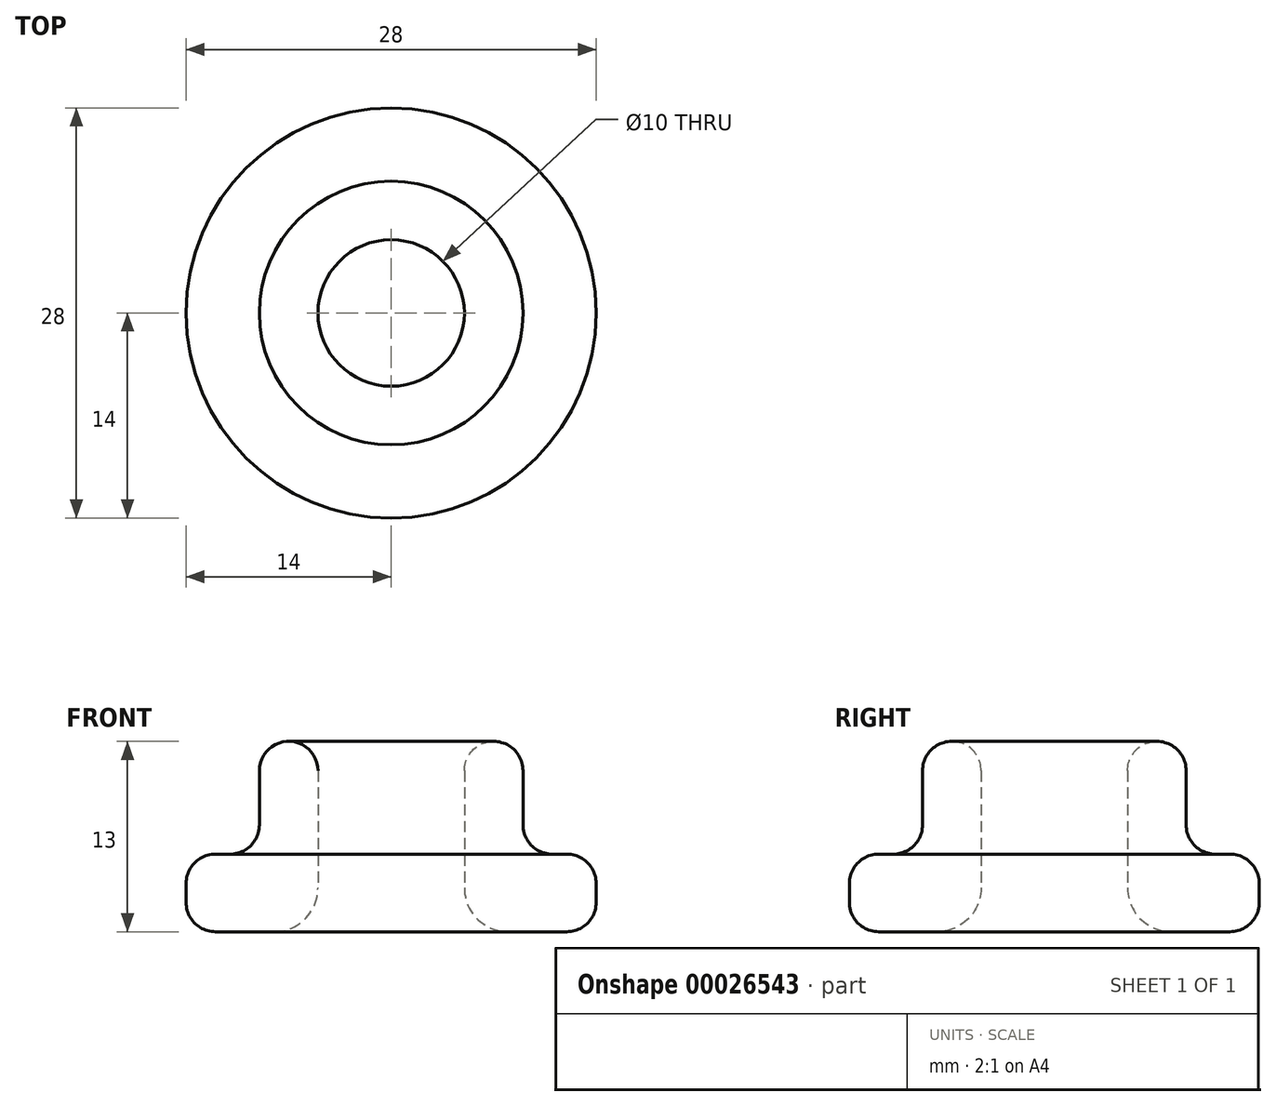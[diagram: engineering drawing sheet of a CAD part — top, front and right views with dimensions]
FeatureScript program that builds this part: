
annotation { "Feature Type Name" : "Feature", "Feature Type Description" : "" }
export const myFeature = defineFeature(function(context is Context, id is Id, definition is map)
    precondition{}
    {
        {
            var Q0;
            Q0=qCreatedBy(makeId("Front.planeOp"),FACE);
            var sketch = newSketch(context, id + "F0", { "sketchPlane" : qUnion([Q0])});
            skLineSegment(sketch, "E0", {"start": v(8, 0) * mm, "end": v(12, 0) * mm});
            skLineSegment(sketch, "E1", {"start": v(14, 2) * mm, "end": v(14, 3.3) * mm});
            skLineSegment(sketch, "E2", {"start": v(12, 5.3) * mm, "end": v(11, 5.3) * mm});
            skLineSegment(sketch, "E3", {"start": v(9, 7.3) * mm, "end": v(9, 11) * mm});
            skLineSegment(sketch, "E4", {"start": v(5, 11) * mm, "end": v(5, 3) * mm});
            skLineSegment(sketch, "E5", {"start": v(0, 0) * mm, "end": v(0, 27.16) * mm, "construction": true});
            skPoint(sketch, "E6.visualSharp", {"position": v(5, 0) * mm});
            skArc(sketch, "E6.filletArc", {"start": v(5, 3) * mm, "mid": v(5.88, 0.88) * mm, "end": v(8, 0) * mm});
            skPoint(sketch, "E7.visualSharp", {"position": v(14, 0) * mm});
            skArc(sketch, "E7.filletArc", {"start": v(12, 0) * mm, "mid": v(13.41, 0.59) * mm, "end": v(14, 2) * mm});
            skPoint(sketch, "E8.visualSharp", {"position": v(14, 5.3) * mm});
            skArc(sketch, "E8.filletArc", {"start": v(14, 3.3) * mm, "mid": v(13.41, 4.71) * mm, "end": v(12, 5.3) * mm});
            skPoint(sketch, "E9.visualSharp", {"position": v(9, 5.3) * mm});
            skArc(sketch, "E9.filletArc", {"start": v(9, 7.3) * mm, "mid": v(9.59, 5.89) * mm, "end": v(11, 5.3) * mm});
            skArc(sketch, "E10", {"start": v(9, 11) * mm, "mid": v(7, 13) * mm, "end": v(5, 11) * mm});
            skSolve(sketch);
        }
        {
            var Q0;
            Q0=makeQuery(id+"F0.imprint","IMPRINT",FACE,{"disambiguationData":[TD([[makeQuery(id+"F0.imprint","IMPRINT",EDGE,{"derivedFrom":sQuery(id+"F0.wireOp",EDGE,"E0")}),1.0]])]});
            var Q1;
            Q1=sQuery(id+"F0.wireOp",EDGE,"E2");
            var Q2;
            Q2=sQuery(id+"F0.wireOp",EDGE,"5344fd15-d4b9-4e76-99fa-d884e4c4a93f");
            var Q3;
            Q3=sQuery(id+"F0.wireOp",EDGE,"E4");
            var Q4;
            Q4=sQuery(id+"F0.wireOp",EDGE,"E3");
            var Q5;
            Q5=sQuery(id+"F0.wireOp",EDGE,"E1");
            var Q6;
            Q6=sQuery(id+"F0.wireOp",EDGE,"E0");
            var Q7;
            Q7=sQuery(id+"F0.wireOp",EDGE,"1340d823-c927-479e-8c55-b1714bb62738");
            var Q8;
            Q8=sQuery(id+"F0.wireOp",EDGE,"E5");
            revolve(context, id + "F1", {"entities" : qUnion([Q0]), "surfaceEntities" : qUnion([Q1, Q2, Q3, Q4, Q5, Q6, Q7]), "axis" : qUnion([Q8]), "revolveType" : RevolveType.FULL});
        }
    });
